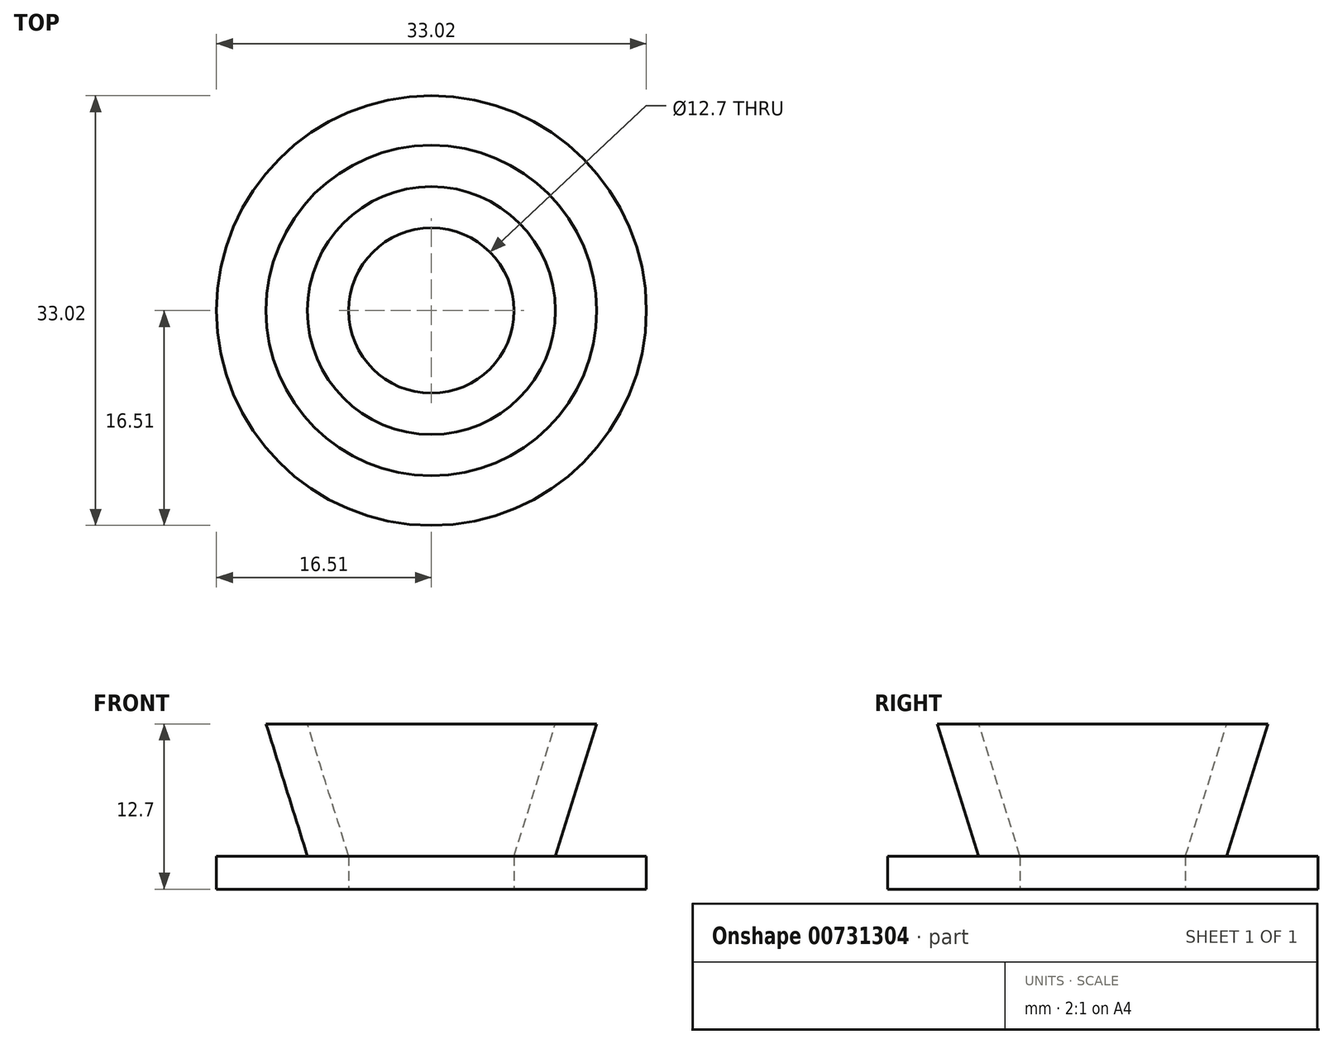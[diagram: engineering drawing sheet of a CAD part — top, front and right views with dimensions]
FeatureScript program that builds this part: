
annotation { "Feature Type Name" : "Feature", "Feature Type Description" : "" }
export const myFeature = defineFeature(function(context is Context, id is Id, definition is map)
    precondition{}
    {
        {
            var Q0;
            Q0=qCreatedBy(makeId("Top.planeOp"),FACE);
            var sketch = newSketch(context, id + "F0", { "sketchPlane" : qUnion([Q0])});
            skCircle(sketch, "E0", {"center": v(0, 0) * mm, "radius": 6.35 * mm});
            skCircle(sketch, "E1", {"center": v(0, 0) * mm, "radius": 16.51 * mm});
            skCircle(sketch, "E2", {"center": v(0, 0) * mm, "radius": 9.53 * mm});
            skSolve(sketch);
        }
        {
            var Q0;
            Q0=qCreatedBy(makeId("Right.planeOp"),FACE);
            var sketch = newSketch(context, id + "F1", { "sketchPlane" : qUnion([Q0])});
            skLineSegment(sketch, "E3.bottom", {"start": v(0, 0) * mm, "end": v(-6.35, 0) * mm});
            skLineSegment(sketch, "E3.top", {"start": v(0, 2.54) * mm, "end": v(-6.35, 2.54) * mm});
            skLineSegment(sketch, "E3.left", {"start": v(0, 0) * mm, "end": v(0, 2.54) * mm});
            skLineSegment(sketch, "E3.right", {"start": v(-6.35, 0) * mm, "end": v(-6.35, 2.54) * mm});
            skLineSegment(sketch, "E4", {"start": v(-6.35, 2.54) * mm, "end": v(-6.35, 12.7) * mm});
            skLineSegment(sketch, "E5", {"start": v(-6.35, 12.7) * mm, "end": v(-12.7, 12.7) * mm});
            skLineSegment(sketch, "E6", {"start": v(-12.7, 12.7) * mm, "end": v(-9.53, 2.54) * mm});
            skLineSegment(sketch, "E7", {"start": v(-9.53, 2.54) * mm, "end": v(-6.35, 2.54) * mm});
            skLineSegment(sketch, "E8", {"start": v(-6.35, 2.54) * mm, "end": v(-9.53, 12.7) * mm});
            skSolve(sketch);
        }
        {
            var Q0;
            Q0=makeQuery(id+"F0.imprint","IMPRINT",FACE,{"disambiguationData":[TD([[makeQuery(id+"F0.imprint","IMPRINT",EDGE,{"derivedFrom":sQuery(id+"F0.wireOp",EDGE,"E1")}),1.0]])]});
            var Q1;
            Q1=makeQuery(id+"F0.imprint","IMPRINT",FACE,{"disambiguationData":[TD([[makeQuery(id+"F0.imprint","IMPRINT",EDGE,{"derivedFrom":sQuery(id+"F0.wireOp",EDGE,"E0")}),-1.0]])]});
            extrude(context, id + "F2", {"entities" : qUnion([Q0, Q1]), "depth" : 2.54 * mm, "offsetDistance" : 25.4 * mm});
        }
        {
            var Q0;
            {var subQ0=sQuery(id+"F1.wireOp",EDGE,"E6");Q0=makeQuery(id+"F1.imprint","IMPRINT",FACE,{"disambiguationData":[TD([[makeQuery(id+"F1.imprint","IMPRINT",EDGE,{"derivedFrom":subQ0}),1.0]])]});}
            var Q1;
            Q1=sQuery(id+"F1.wireOp",EDGE,"E3.left");
            revolve(context, id + "F3", {"surfaceOperationType" : NewSurfaceOperationType.NEW, "entities" : qUnion([Q0]), "axis" : qUnion([Q1]), "revolveType" : RevolveType.FULL});
        }
    });
